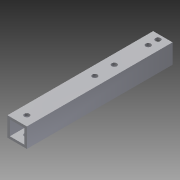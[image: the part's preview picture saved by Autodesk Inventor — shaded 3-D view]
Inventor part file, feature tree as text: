
AUTODESK INVENTOR PART (.ipt)
format: ipt  version: 2013 (Build 170138000, 138)  size: 112,128 bytes
history: native  units: in
note: dims shown in document units (in); Inventor stores cm internally (conversion verified against a paired STEP export)
features: extrude x4, sketch x4, reference x4
ambient origin geometry x8: Origin, YZ Plane, XZ Plane, XY Plane, X Axis, Y Axis, Z Axis, Center Point
bodies: Solid1 (feature_tree)
feature tree (12):
  extrude  "Extrusion1"  Depth=1.0in
  extrude  "Extrusion2"  Depth=7.5in TaperAngle=0.0deg
  extrude  "Extrusion3"  Depth=1.0in TaperAngle=0.0deg
  extrude  "Extrusion4"  [1 undecoded]
  sketch  "Sketch1"  dims[d0=1.0in d2=1.0in]
  sketch  "Sketch2"  dims[d3=0.125in d4=7.5in d5=0.0in]
  reference  "Reference1"
  reference  "Reference2"
  sketch  "Sketch3"  dims[d6=1.0in d7=0.0in d8=1.0in d9=0.0in]
  reference  "Reference3"
  reference  "Reference4"
  sketch  "Sketch4"  dims[d10=1.0in d11=0.0in]
note: 1 required parameter value undecoded (feature->parameter linkage not recoverable at this tier; creation-order binding heuristic only, values carry confidence <= 0.55)
